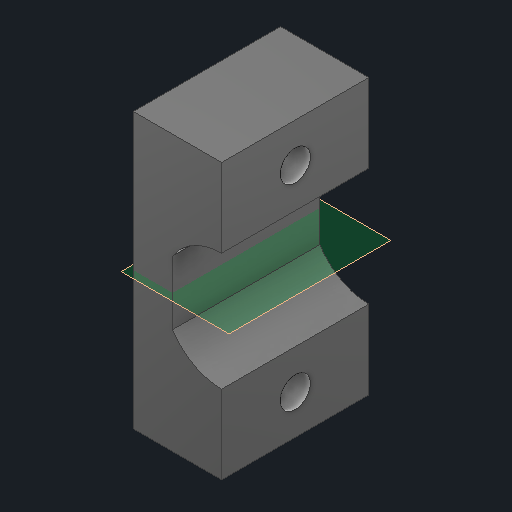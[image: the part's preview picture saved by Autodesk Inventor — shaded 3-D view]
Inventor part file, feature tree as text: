
AUTODESK INVENTOR PART (.ipt)
format: ipt  version: 2024 (Build 280153000, 153)  size: 116,224 bytes
history: native  units: in
note: dims shown in document units (in); Inventor stores cm internally (conversion verified against a paired STEP export)
features: other x3, sketch x1, plane x1
ambient origin geometry x8: Origin, YZ Plane, XZ Plane, XY Plane, X Axis, Y Axis, Z Axis, Center Point
bodies: Body1 (feature_tree)
feature tree (5):
  other  "podstawka silnika.ipt"
  other  "Solid2::podstawka silnika.ipt"
  other  "TaggingFeature1"
  sketch  "Sketch3"  dims[d0=0.3937in]
  plane  "Work Plane1"
